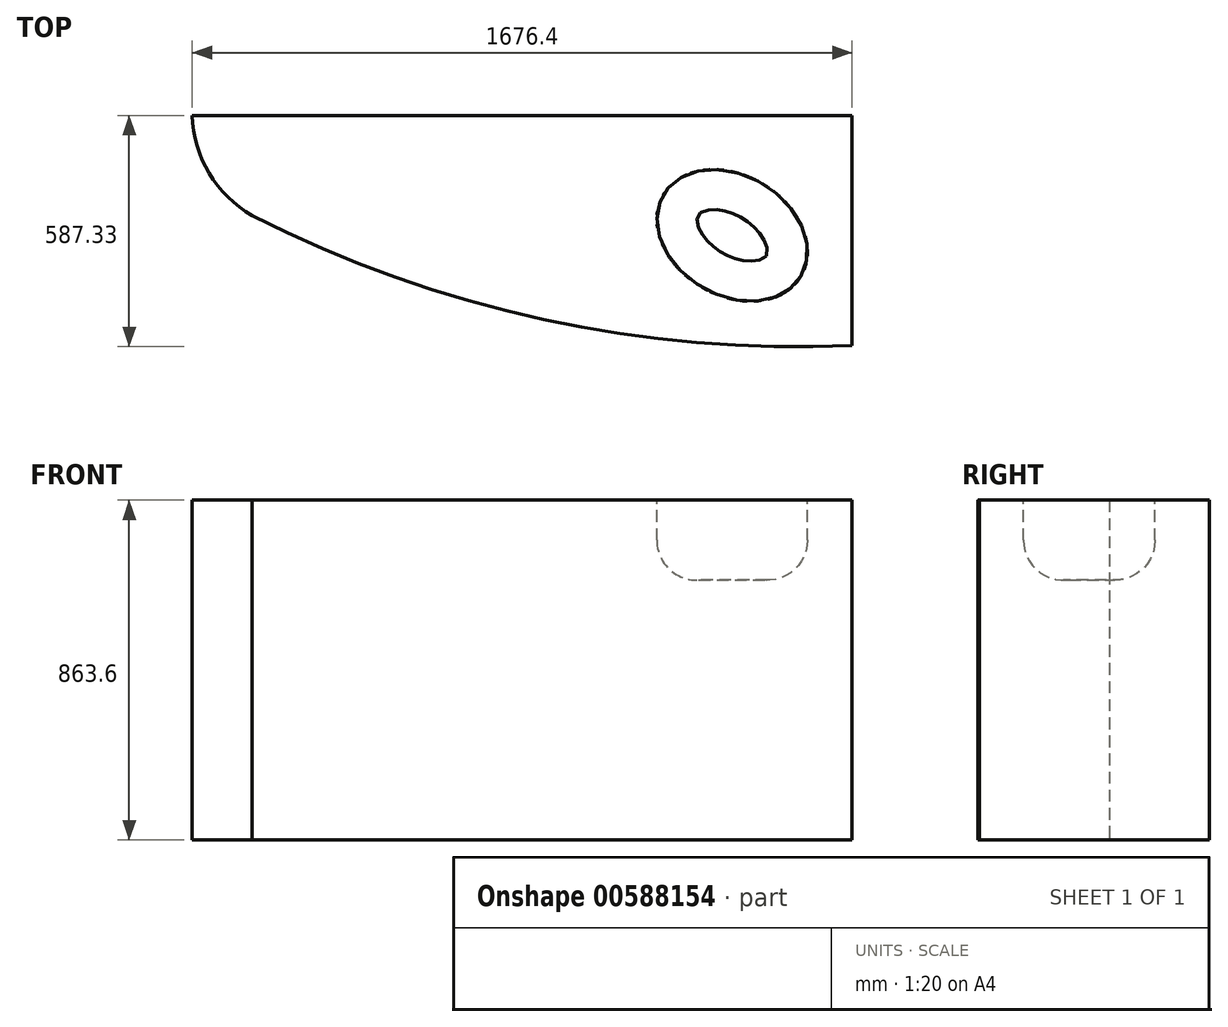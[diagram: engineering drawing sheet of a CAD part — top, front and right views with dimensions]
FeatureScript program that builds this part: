
annotation { "Feature Type Name" : "Feature", "Feature Type Description" : "" }
export const myFeature = defineFeature(function(context is Context, id is Id, definition is map)
    precondition{}
    {
        {
            var Q0;
            Q0=qCreatedBy(makeId("Top.planeOp"),FACE);
            var sketch = newSketch(context, id + "F0", { "sketchPlane" : qUnion([Q0])});
            skLineSegment(sketch, "E0.bottom", {"start": v(0, 0) * mm, "end": v(-1524, 0) * mm});
            skLineSegment(sketch, "E0.left", {"start": v(0, 0) * mm, "end": v(0, -584.2) * mm});
            skArc(sketch, "E1", {"start": v(-1524, -254) * mm, "mid": v(-783.47, -518.2) * mm, "end": v(0, -584.2) * mm});
            skArc(sketch, "E2", {"start": v(-1676.4, 0) * mm, "mid": v(-1633.13, -146.76) * mm, "end": v(-1524, -254) * mm});
            skLineSegment(sketch, "E3", {"start": v(-1676.4, 0) * mm, "end": v(-1524, 0) * mm});
            skSolve(sketch);
        }
        {
            var Q0;
            Q0=makeQuery(id+"F0.imprint","IMPRINT",FACE,{"disambiguationData":[TD([[makeQuery(id+"F0.imprint","IMPRINT",EDGE,{"derivedFrom":sQuery(id+"F0.wireOp",EDGE,"E0.bottom")}),1.0]])]});
            extrude(context, id + "F1", {"entities" : qUnion([Q0]), "depth" : 863.6 * mm, "offsetDistance" : 25.4 * mm});
        }
        {
            var Q0;
            Q0=makeQuery(id+"F1.opExtrude","CAP_FACE",FACE,{"disambiguationData":[OSD([sQuery(id+"F0.wireOp",EDGE,"E0.bottom"),sQuery(id+"F0.wireOp",EDGE,"E0.left"),sQuery(id+"F0.wireOp",EDGE,"E0.right"),sQuery(id+"F0.wireOp",EDGE,"E1")])],"isStart":false});
            var sketch = newSketch(context, id + "F2", { "sketchPlane" : qUnion([Q0])});
            skEllipse(sketch, "E4", {"center": v(-304.8, -304.8) * mm, "majorRadius": 203.2 * mm, "minorRadius": 152.4 * mm, "majorAxis": v(0.86, -0.5)});
            skSolve(sketch);
        }
        {
            var Q0;
            Q0=makeQuery(id+"F2.imprint","IMPRINT",FACE,{"disambiguationData":[TD([[makeQuery(id+"F2.imprint","IMPRINT",EDGE,{"derivedFrom":sQuery(id+"F2.wireOp",EDGE,"E4")}),1.0]])]});
            extrude(context, id + "F3", {"entities" : qUnion([Q0]), "operationType" : NewBodyOperationType.REMOVE, "oppositeDirection" : true, "depth" : 203.2 * mm, "offsetDistance" : 25.4 * mm});
        }
        {
            var Q0;
            Q0=makeQuery(id+"F3.boolean.opBoolean","COPY",FACE,{"derivedFrom":makeQuery(id+"F3.opExtrude","CAP_FACE",FACE,{"disambiguationData":[OSD([sQuery(id+"F2.wireOp",EDGE,"E4")])],"isStart":false})});
            fillet(context, id + "F4", {"entities" : qUnion([Q0]), "radius" : 101.6 * mm, "tangentPropagation" : true, "allowEdgeOverflow" : false});
        }
    });
